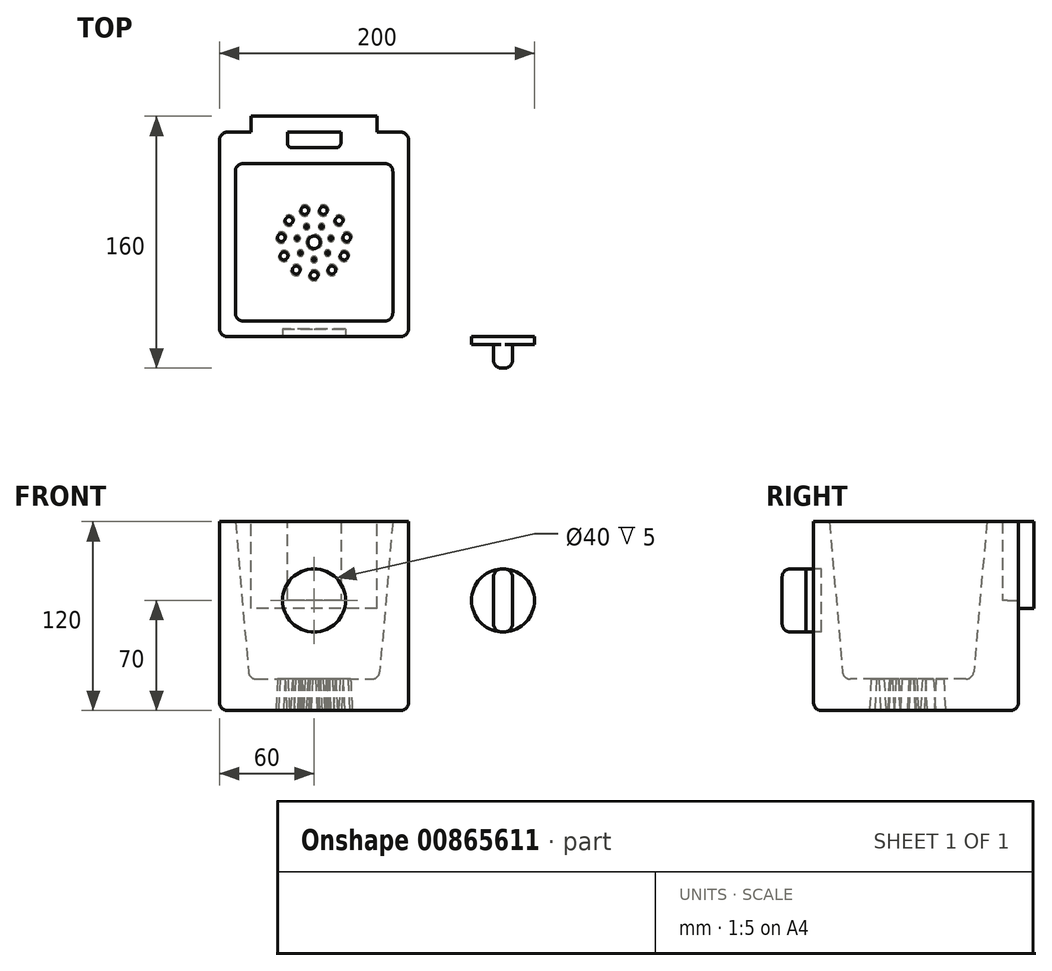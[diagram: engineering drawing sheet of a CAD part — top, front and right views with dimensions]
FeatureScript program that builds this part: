
annotation { "Feature Type Name" : "Feature", "Feature Type Description" : "" }
export const myFeature = defineFeature(function(context is Context, id is Id, definition is map)
    precondition{}
    {
        {
            assignVariable(context, id + "F0", {"name" : "length", "anyValue" : 120});
        }
        {
            var Q0;
            Q0=qCreatedBy(makeId("Top.planeOp"),FACE);
            var sketch = newSketch(context, id + "F1", { "sketchPlane" : qUnion([Q0])});
            skLineSegment(sketch, "E0.bottom", {"start": v(60, 60) * mm, "end": v(-60, 60) * mm});
            skLineSegment(sketch, "E0.top", {"start": v(60, -60) * mm, "end": v(-60, -60) * mm});
            skLineSegment(sketch, "E0.left", {"start": v(60, 60) * mm, "end": v(60, -60) * mm});
            skLineSegment(sketch, "E0.right", {"start": v(-60, 60) * mm, "end": v(-60, -60) * mm});
            skPoint(sketch, "E0.middle", {"position": v(0, 0) * mm});
            skSolve(sketch);
        }
        {
            var Q0;
            Q0=makeQuery(id+"F1.imprint","IMPRINT",FACE,{"disambiguationData":[TD([[makeQuery(id+"F1.imprint","IMPRINT",EDGE,{"derivedFrom":sQuery(id+"F1.wireOp",EDGE,"E0.bottom")}),1.0]])]});
            extrude(context, id + "F2", {"entities" : qUnion([Q0]), "depth" : (getVariable(context, 'length')) * mm, "offsetDistance" : 25 * mm});
        }
        {
            var Q0;
            Q0=makeQuery(id+"F2.opExtrude","SWEPT_FACE",FACE,{"disambiguationData":[OSD([sQuery(id+"F1.wireOp",EDGE,"E0.bottom")])]});
            var sketch = newSketch(context, id + "F3", { "sketchPlane" : qUnion([Q0])});
            skLineSegment(sketch, "E1.bottom", {"start": v(-60, 0) * mm, "end": v(60, 0) * mm});
            skLineSegment(sketch, "E1.top", {"start": v(-60, 216) * mm, "end": v(60, 216) * mm});
            skLineSegment(sketch, "E1.left", {"start": v(-60, 0) * mm, "end": v(-60, 216) * mm});
            skLineSegment(sketch, "E1.right", {"start": v(60, 0) * mm, "end": v(60, 216) * mm});
            skSolve(sketch);
        }
        {
            var Q0;
            Q0=makeQuery(id+"F2.opExtrude","CAP_FACE",FACE,{"disambiguationData":[OSD([sQuery(id+"F1.wireOp",EDGE,"E0.bottom"),sQuery(id+"F1.wireOp",EDGE,"E0.top"),sQuery(id+"F1.wireOp",EDGE,"E0.left"),sQuery(id+"F1.wireOp",EDGE,"E0.right")])],"isStart":false});
            var sketch = newSketch(context, id + "F4", { "sketchPlane" : qUnion([Q0])});
            skLineSegment(sketch, "E2.bottom", {"start": v(50, 50) * mm, "end": v(-50, 50) * mm});
            skLineSegment(sketch, "E2.top", {"start": v(50, -50) * mm, "end": v(-50, -50) * mm});
            skLineSegment(sketch, "E2.left", {"start": v(50, 50) * mm, "end": v(50, -50) * mm});
            skLineSegment(sketch, "E2.right", {"start": v(-50, 50) * mm, "end": v(-50, -50) * mm});
            skPoint(sketch, "E2.middle", {"position": v(0, 0) * mm});
            skSolve(sketch);
        }
        {
            var Q0;
            Q0=makeQuery(id+"F4.imprint","IMPRINT",FACE,{"disambiguationData":[TD([[makeQuery(id+"F4.imprint","IMPRINT",EDGE,{"derivedFrom":sQuery(id+"F4.wireOp",EDGE,"E2.bottom")}),1.0]])]});
            extrude(context, id + "F5", {"entities" : qUnion([Q0]), "operationType" : NewBodyOperationType.REMOVE, "oppositeDirection" : true, "depth" : 100 * mm, "offsetDistance" : 25 * mm, "hasDraft" : true, "draftAngle" : 5 * degree, "draftPullDirection" : true});
        }
        {
            var Q0;
            {var subQ0=sQuery(id+"F3.wireOp",EDGE,"E1.bottom");Q0=makeQuery(id+"F3.imprint","IMPRINT",FACE,{"disambiguationData":[TD([[makeQuery(id+"F3.imprint","IMPRINT",EDGE,{"derivedFrom":subQ0}),1.0]])]});}
            var Q1;
            {var subQ0=sQuery(id+"F3.wireOp",EDGE,"E1.top");Q1=makeQuery(id+"F3.imprint","IMPRINT",FACE,{"disambiguationData":[TD([[makeQuery(id+"F3.imprint","IMPRINT",EDGE,{"derivedFrom":subQ0}),-1.0]])]});}
            extrude(context, id + "F6", {"entities" : qUnion([Q0, Q1]), "operationType" : NewBodyOperationType.ADD, "depth" : 10 * mm, "offsetDistance" : 25 * mm});
        }
        {
            var Q0;
            Q0=makeQuery(id+"F6.opExtrude","CAP_FACE",FACE,{"disambiguationData":[OSD([sQuery(id+"F3.wireOp",EDGE,"E1.bottom"),sQuery(id+"F3.wireOp",EDGE,"E1.top"),sQuery(id+"F3.wireOp",EDGE,"E1.left"),sQuery(id+"F3.wireOp",EDGE,"E1.right")])],"isStart":true});
            var sketch = newSketch(context, id + "F7", { "sketchPlane" : qUnion([Q0])});
            skLineSegment(sketch, "E3", {"start": v(0, 223.83) * mm, "end": v(0, 211) * mm, "construction": true});
            skPoint(sketch, "E3.startSnap0", {"position": v(0, 216) * mm});
            skLineSegment(sketch, "E4.bottom", {"start": v(0, 194) * mm, "end": v(-45, 194) * mm});
            skLineSegment(sketch, "E4.top", {"start": v(0, 184) * mm, "end": v(-45, 184) * mm});
            skLineSegment(sketch, "E4.left", {"start": v(0, 194) * mm, "end": v(0, 184) * mm});
            skLineSegment(sketch, "E4.right", {"start": v(-45, 194) * mm, "end": v(-45, 184) * mm});
            skLineSegment(sketch, "E5.bottom", {"start": v(-45, 179) * mm, "end": v(-20, 179) * mm});
            skLineSegment(sketch, "E5.top", {"start": v(-45, 169) * mm, "end": v(-20, 169) * mm});
            skLineSegment(sketch, "E5.left", {"start": v(-45, 179) * mm, "end": v(-45, 169) * mm});
            skLineSegment(sketch, "E5.right", {"start": v(-20, 179) * mm, "end": v(-20, 169) * mm});
            skLineSegment(sketch, "E6.bottom", {"start": v(-45, 164) * mm, "end": v(0, 164) * mm});
            skLineSegment(sketch, "E6.top", {"start": v(-45, 154) * mm, "end": v(0, 154) * mm});
            skLineSegment(sketch, "E6.left", {"start": v(-45, 164) * mm, "end": v(-45, 154) * mm});
            skLineSegment(sketch, "E6.right", {"start": v(0, 164) * mm, "end": v(0, 154) * mm});
            skLineSegment(sketch, "E7.bottom", {"start": v(-45, 149) * mm, "end": v(-35, 149) * mm});
            skLineSegment(sketch, "E7.top", {"start": v(-45, 129) * mm, "end": v(-35, 129) * mm});
            skLineSegment(sketch, "E7.left", {"start": v(-45, 149) * mm, "end": v(-45, 129) * mm});
            skLineSegment(sketch, "E7.right", {"start": v(-35, 149) * mm, "end": v(-35, 139) * mm});
            skLineSegment(sketch, "E8.bottom", {"start": v(-35, 139) * mm, "end": v(0, 139) * mm});
            skLineSegment(sketch, "E8.top", {"start": v(-35, 129) * mm, "end": v(0, 129) * mm});
            skLineSegment(sketch, "E8.right", {"start": v(0, 139) * mm, "end": v(0, 129) * mm});
            skLineSegment(sketch, "E9.bottom", {"start": v(-28, 149) * mm, "end": v(0, 149) * mm});
            skLineSegment(sketch, "E9.top", {"start": v(-28, 144) * mm, "end": v(0, 144) * mm});
            skLineSegment(sketch, "E9.left", {"start": v(-28, 149) * mm, "end": v(-28, 144) * mm});
            skLineSegment(sketch, "E9.right", {"start": v(0, 149) * mm, "end": v(0, 144) * mm});
            skLineSegment(sketch, "E10.bottom", {"start": v(-45, 211) * mm, "end": v(-35, 211) * mm});
            skLineSegment(sketch, "E10.top", {"start": v(-45, 198) * mm, "end": v(-35, 198) * mm});
            skLineSegment(sketch, "E10.left", {"start": v(-45, 211) * mm, "end": v(-45, 198) * mm});
            skLineSegment(sketch, "E10.right", {"start": v(-35, 211) * mm, "end": v(-35, 198) * mm});
            skLineSegment(sketch, "E11.bottom", {"start": v(0, 211) * mm, "end": v(-25, 211) * mm});
            skLineSegment(sketch, "E11.top", {"start": v(0, 198) * mm, "end": v(-25, 198) * mm});
            skLineSegment(sketch, "E11.left", {"start": v(0, 211) * mm, "end": v(0, 198) * mm});
            skLineSegment(sketch, "E11.right", {"start": v(-25, 211) * mm, "end": v(-25, 198) * mm});
            skArc(sketch, "E12", {"start": v(0, 180.92) * mm, "mid": v(-6.92, 174) * mm, "end": v(0, 167.08) * mm});
            skPoint(sketch, "E12.centerSnap0", {"position": v(-20, 174) * mm});
            skLineSegment(sketch, "E13.trimOffspring", {"start": v(0, 154) * mm, "end": v(0, 149) * mm, "construction": true});
            skLineSegment(sketch, "E14.trimOffspring", {"start": v(0, 144) * mm, "end": v(0, 139) * mm, "construction": true});
            skLineSegment(sketch, "E15.trimOffspring", {"start": v(0, 129) * mm, "end": v(0, 105.75) * mm, "construction": true});
            skLineSegment(sketch, "E16.trimOffspring", {"start": v(0, 184) * mm, "end": v(0, 164) * mm, "construction": true});
            skLineSegment(sketch, "E17.trimOffspring", {"start": v(0, 198) * mm, "end": v(0, 194) * mm, "construction": true});
            skArc(sketch, "E18.MirrorCS", {"start": v(0, 180.92) * mm, "mid": v(6.92, 174) * mm, "end": v(0, 167.08) * mm});
            skLineSegment(sketch, "E19.MirrorCS", {"start": v(28, 149) * mm, "end": v(28, 144) * mm});
            skLineSegment(sketch, "E20.MirrorCS", {"start": v(20, 179) * mm, "end": v(20, 169) * mm});
            skLineSegment(sketch, "E21.MirrorCS", {"start": v(35, 211) * mm, "end": v(35, 198) * mm});
            skLineSegment(sketch, "E22.MirrorCS", {"start": v(45, 169) * mm, "end": v(20, 169) * mm});
            skPoint(sketch, "E23.MirrorP", {"position": v(20, 174) * mm});
            skLineSegment(sketch, "E24.MirrorCS", {"start": v(45, 179) * mm, "end": v(20, 179) * mm});
            skLineSegment(sketch, "E25.MirrorCS", {"start": v(0, 211) * mm, "end": v(25, 211) * mm});
            skLineSegment(sketch, "E26.MirrorCS", {"start": v(28, 144) * mm, "end": v(0, 144) * mm});
            skLineSegment(sketch, "E27.MirrorCS", {"start": v(45, 154) * mm, "end": v(0, 154) * mm});
            skLineSegment(sketch, "E28.MirrorCS", {"start": v(45, 129) * mm, "end": v(35, 129) * mm});
            skLineSegment(sketch, "E29.MirrorCS", {"start": v(45, 179) * mm, "end": v(45, 169) * mm});
            skLineSegment(sketch, "E30.MirrorCS", {"start": v(0, 194) * mm, "end": v(45, 194) * mm});
            skLineSegment(sketch, "E31.MirrorCS", {"start": v(45, 149) * mm, "end": v(35, 149) * mm});
            skLineSegment(sketch, "E32.MirrorCS", {"start": v(35, 149) * mm, "end": v(35, 139) * mm});
            skLineSegment(sketch, "E33.MirrorCS", {"start": v(45, 211) * mm, "end": v(35, 211) * mm});
            skLineSegment(sketch, "E34.MirrorCS", {"start": v(25, 211) * mm, "end": v(25, 198) * mm});
            skLineSegment(sketch, "E35.MirrorCS", {"start": v(45, 198) * mm, "end": v(35, 198) * mm});
            skLineSegment(sketch, "E36.MirrorCS", {"start": v(35, 129) * mm, "end": v(0, 129) * mm});
            skLineSegment(sketch, "E37.MirrorCS", {"start": v(45, 164) * mm, "end": v(0, 164) * mm});
            skLineSegment(sketch, "E38.MirrorCS", {"start": v(35, 139) * mm, "end": v(0, 139) * mm});
            skLineSegment(sketch, "E39.MirrorCS", {"start": v(28, 149) * mm, "end": v(0, 149) * mm});
            skLineSegment(sketch, "E40.MirrorCS", {"start": v(0, 184) * mm, "end": v(45, 184) * mm});
            skLineSegment(sketch, "E41.MirrorCS", {"start": v(45, 164) * mm, "end": v(45, 154) * mm});
            skLineSegment(sketch, "E42.MirrorCS", {"start": v(45, 211) * mm, "end": v(45, 198) * mm});
            skLineSegment(sketch, "E43.MirrorCS", {"start": v(0, 198) * mm, "end": v(25, 198) * mm});
            skLineSegment(sketch, "E44.MirrorCS", {"start": v(45, 149) * mm, "end": v(45, 129) * mm});
            skLineSegment(sketch, "E45.MirrorCS", {"start": v(45, 194) * mm, "end": v(45, 184) * mm});
            skSolve(sketch);
        }
        {
            var Q0;
            Q0=makeQuery(id+"F7.imprint","IMPRINT",FACE,{"disambiguationData":[TD([[makeQuery(id+"F7.imprint","IMPRINT",EDGE,{"derivedFrom":sQuery(id+"F7.wireOp",EDGE,"E7.bottom")}),-1.0]])]});
            var Q1;
            Q1=makeQuery(id+"F7.imprint","IMPRINT",FACE,{"disambiguationData":[TD([[makeQuery(id+"F7.imprint","IMPRINT",EDGE,{"derivedFrom":sQuery(id+"F7.wireOp",EDGE,"E9.bottom")}),-1.0]])]});
            var Q2;
            Q2=makeQuery(id+"F7.imprint","IMPRINT",FACE,{"disambiguationData":[TD([[makeQuery(id+"F7.imprint","IMPRINT",EDGE,{"derivedFrom":sQuery(id+"F7.wireOp",EDGE,"E8.right")}),1.0]])]});
            var Q3;
            Q3=makeQuery(id+"F7.imprint","IMPRINT",FACE,{"disambiguationData":[TD([[makeQuery(id+"F7.imprint","IMPRINT",EDGE,{"derivedFrom":sQuery(id+"F7.wireOp",EDGE,"E9.right")}),1.0]])]});
            var Q4;
            Q4=makeQuery(id+"F7.imprint","IMPRINT",FACE,{"disambiguationData":[TD([[makeQuery(id+"F7.imprint","IMPRINT",EDGE,{"derivedFrom":sQuery(id+"F7.wireOp",EDGE,"E6.bottom")}),-1.0]])]});
            var Q5;
            Q5=makeQuery(id+"F7.imprint","IMPRINT",FACE,{"disambiguationData":[TD([[makeQuery(id+"F7.imprint","IMPRINT",EDGE,{"derivedFrom":sQuery(id+"F7.wireOp",EDGE,"E5.bottom")}),-1.0]])]});
            var Q6;
            Q6=makeQuery(id+"F7.imprint","IMPRINT",FACE,{"disambiguationData":[TD([[makeQuery(id+"F7.imprint","IMPRINT",EDGE,{"derivedFrom":sQuery(id+"F7.wireOp",EDGE,"E4.bottom")}),1.0]])]});
            var Q7;
            Q7=makeQuery(id+"F7.imprint","IMPRINT",FACE,{"disambiguationData":[TD([[makeQuery(id+"F7.imprint","IMPRINT",EDGE,{"derivedFrom":sQuery(id+"F7.wireOp",EDGE,"E10.bottom")}),-1.0]])]});
            var Q8;
            Q8=makeQuery(id+"F7.imprint","IMPRINT",FACE,{"disambiguationData":[TD([[makeQuery(id+"F7.imprint","IMPRINT",EDGE,{"derivedFrom":sQuery(id+"F7.wireOp",EDGE,"E11.bottom")}),1.0]])]});
            var Q9;
            Q9=makeQuery(id+"F7.imprint","IMPRINT",FACE,{"disambiguationData":[TD([[makeQuery(id+"F7.imprint","IMPRINT",EDGE,{"derivedFrom":sQuery(id+"F7.wireOp",EDGE,"E11.left")}),1.0]])]});
            var Q10;
            Q10=makeQuery(id+"F7.imprint","IMPRINT",FACE,{"disambiguationData":[TD([[makeQuery(id+"F7.imprint","IMPRINT",EDGE,{"derivedFrom":sQuery(id+"F7.wireOp",EDGE,"E21.MirrorCS")}),1.0]])]});
            var Q11;
            Q11=makeQuery(id+"F7.imprint","IMPRINT",FACE,{"disambiguationData":[TD([[makeQuery(id+"F7.imprint","IMPRINT",EDGE,{"derivedFrom":sQuery(id+"F7.wireOp",EDGE,"E4.left")}),1.0]])]});
            var Q12;
            Q12=makeQuery(id+"F7.imprint","IMPRINT",FACE,{"disambiguationData":[TD([[makeQuery(id+"F7.imprint","IMPRINT",EDGE,{"derivedFrom":sQuery(id+"F7.wireOp",EDGE,"E20.MirrorCS")}),1.0]])]});
            var Q13;
            Q13=makeQuery(id+"F7.imprint","IMPRINT",FACE,{"disambiguationData":[TD([[makeQuery(id+"F7.imprint","IMPRINT",EDGE,{"derivedFrom":sQuery(id+"F7.wireOp",EDGE,"E12")}),1.0]])]});
            var Q14;
            Q14=makeQuery(id+"F7.imprint","IMPRINT",FACE,{"disambiguationData":[TD([[makeQuery(id+"F7.imprint","IMPRINT",EDGE,{"derivedFrom":sQuery(id+"F7.wireOp",EDGE,"E6.right")}),1.0]])]});
            var Q15;
            Q15=makeQuery(id+"F6.opExtrude","CAP_FACE",FACE,{"disambiguationData":[OSD([sQuery(id+"F3.wireOp",EDGE,"E1.bottom"),sQuery(id+"F3.wireOp",EDGE,"E1.top"),sQuery(id+"F3.wireOp",EDGE,"E1.left"),sQuery(id+"F3.wireOp",EDGE,"E1.right")])],"isStart":false});
            extrude(context, id + "F8", {"entities" : qUnion([Q0, Q1, Q2, Q3, Q4, Q5, Q6, Q7, Q8, Q9, Q10, Q11, Q12, Q13, Q14]), "operationType" : NewBodyOperationType.REMOVE, "endBound" : BoundingType.UP_TO_SURFACE, "oppositeDirection" : true, "depth" : 25 * mm, "endBoundEntityFace" : qUnion([Q15]), "offsetDistance" : 25 * mm});
        }
        {
            var Q0;
            Q0=makeQuery(id+"F6.opExtrude","SWEPT_FACE",FACE,{"disambiguationData":[OSD([sQuery(id+"F3.wireOp",EDGE,"E1.top")])]});
            var sketch = newSketch(context, id + "F9", { "sketchPlane" : qUnion([Q0])});
            skLineSegment(sketch, "E46.bottom", {"start": v(-60, 70) * mm, "end": v(60, 70) * mm});
            skLineSegment(sketch, "E46.top", {"start": v(-60, -60) * mm, "end": v(60, -60) * mm});
            skLineSegment(sketch, "E46.left", {"start": v(-60, 70) * mm, "end": v(-60, -60) * mm});
            skLineSegment(sketch, "E46.right", {"start": v(60, 70) * mm, "end": v(60, -60) * mm});
            skSolve(sketch);
        }
        {
            var Q0;
            Q0=qSketchRegion(id+"F9",true);
            extrude(context, id + "F10", {"entities" : qUnion([Q0]), "operationType" : NewBodyOperationType.ADD, "depth" : 25 * mm, "offsetDistance" : 25 * mm, "hasDraft" : true, "draftAngle" : 10 * degree, "draftPullDirection" : true});
        }
        {
            var Q0;
            Q0=makeQuery(id+"F10.opExtrude","CAP_FACE",FACE,{"disambiguationData":[OSD([sQuery(id+"F9.wireOp",EDGE,"E46.bottom"),sQuery(id+"F9.wireOp",EDGE,"E46.top"),sQuery(id+"F9.wireOp",EDGE,"E46.left"),sQuery(id+"F9.wireOp",EDGE,"E46.right")])],"isStart":false});
            var sketch = newSketch(context, id + "F11", { "sketchPlane" : qUnion([Q0])});
            skLineSegment(sketch, "E47.bottom", {"start": v(-45.6, 55.6) * mm, "end": v(45.6, 55.6) * mm});
            skLineSegment(sketch, "E47.top", {"start": v(-45.6, -45.6) * mm, "end": v(45.6, -45.6) * mm});
            skLineSegment(sketch, "E47.left", {"start": v(-45.6, 55.6) * mm, "end": v(-45.6, -45.6) * mm});
            skLineSegment(sketch, "E47.right", {"start": v(45.6, 55.6) * mm, "end": v(45.6, -45.6) * mm});
            skSolve(sketch);
        }
        {
            var Q0;
            Q0=makeQuery(id+"F11.imprint","IMPRINT",FACE,{"disambiguationData":[TD([[makeQuery(id+"F11.imprint","IMPRINT",EDGE,{"derivedFrom":sQuery(id+"F11.wireOp",EDGE,"E47.bottom")}),-1.0]])]});
            extrude(context, id + "F12", {"entities" : qUnion([Q0]), "operationType" : NewBodyOperationType.REMOVE, "oppositeDirection" : true, "depth" : 10 * mm, "offsetDistance" : 25 * mm, "hasDraft" : true, "draftAngle" : 7 * degree, "draftPullDirection" : true});
        }
        {
            var Q0;
            Q0=makeQuery(id+"F12.boolean.opBoolean","COPY",FACE,{"derivedFrom":makeQuery(id+"F12.opExtrude","CAP_FACE",FACE,{"disambiguationData":[OSD([sQuery(id+"F11.wireOp",EDGE,"E47.bottom"),sQuery(id+"F11.wireOp",EDGE,"E47.top"),sQuery(id+"F11.wireOp",EDGE,"E47.left"),sQuery(id+"F11.wireOp",EDGE,"E47.right")])],"isStart":false})});
            var sketch = newSketch(context, id + "F13", { "sketchPlane" : qUnion([Q0])});
            skLineSegment(sketch, "E48.bottom", {"start": v(-44.36, 54.36) * mm, "end": v(44.36, 54.36) * mm});
            skLineSegment(sketch, "E48.top", {"start": v(-44.36, 51.36) * mm, "end": v(44.36, 51.36) * mm});
            skLineSegment(sketch, "E48.left", {"start": v(-44.36, 54.36) * mm, "end": v(-44.36, 51.36) * mm});
            skLineSegment(sketch, "E48.right", {"start": v(44.36, 54.36) * mm, "end": v(44.36, 51.36) * mm});
            skLineSegment(sketch, "E49.0.1.0", {"start": v(-44.36, 46.36) * mm, "end": v(44.36, 46.36) * mm});
            skLineSegment(sketch, "E49.0.1.1", {"start": v(44.36, 49.36) * mm, "end": v(44.36, 46.36) * mm});
            skLineSegment(sketch, "E49.0.1.2", {"start": v(-44.36, 49.36) * mm, "end": v(44.36, 49.36) * mm});
            skLineSegment(sketch, "E49.0.1.3", {"start": v(-44.36, 49.36) * mm, "end": v(-44.36, 46.36) * mm});
            skLineSegment(sketch, "E49.0.2.0", {"start": v(-44.36, 41.36) * mm, "end": v(44.36, 41.36) * mm});
            skLineSegment(sketch, "E49.0.2.1", {"start": v(44.36, 44.36) * mm, "end": v(44.36, 41.36) * mm});
            skLineSegment(sketch, "E49.0.2.2", {"start": v(-44.36, 44.36) * mm, "end": v(44.36, 44.36) * mm});
            skLineSegment(sketch, "E49.0.2.3", {"start": v(-44.36, 44.36) * mm, "end": v(-44.36, 41.36) * mm});
            skLineSegment(sketch, "E49.0.3.0", {"start": v(-44.36, 36.36) * mm, "end": v(44.36, 36.36) * mm});
            skLineSegment(sketch, "E49.0.3.1", {"start": v(44.36, 39.36) * mm, "end": v(44.36, 36.36) * mm});
            skLineSegment(sketch, "E49.0.3.2", {"start": v(-44.36, 39.36) * mm, "end": v(44.36, 39.36) * mm});
            skLineSegment(sketch, "E49.0.3.3", {"start": v(-44.36, 39.36) * mm, "end": v(-44.36, 36.36) * mm});
            skLineSegment(sketch, "E49.0.4.0", {"start": v(-44.36, 31.36) * mm, "end": v(44.36, 31.36) * mm});
            skLineSegment(sketch, "E49.0.4.1", {"start": v(44.36, 34.36) * mm, "end": v(44.36, 31.36) * mm});
            skLineSegment(sketch, "E49.0.4.2", {"start": v(-44.36, 34.36) * mm, "end": v(44.36, 34.36) * mm});
            skLineSegment(sketch, "E49.0.4.3", {"start": v(-44.36, 34.36) * mm, "end": v(-44.36, 31.36) * mm});
            skLineSegment(sketch, "E49.0.5.0", {"start": v(-44.36, 26.36) * mm, "end": v(44.36, 26.36) * mm});
            skLineSegment(sketch, "E49.0.5.1", {"start": v(44.36, 29.36) * mm, "end": v(44.36, 26.36) * mm});
            skLineSegment(sketch, "E49.0.5.2", {"start": v(-44.36, 29.36) * mm, "end": v(44.36, 29.36) * mm});
            skLineSegment(sketch, "E49.0.5.3", {"start": v(-44.36, 29.36) * mm, "end": v(-44.36, 26.36) * mm});
            skLineSegment(sketch, "E49.0.6.0", {"start": v(-44.36, 21.36) * mm, "end": v(44.36, 21.36) * mm});
            skLineSegment(sketch, "E49.0.6.1", {"start": v(44.36, 24.36) * mm, "end": v(44.36, 21.36) * mm});
            skLineSegment(sketch, "E49.0.6.2", {"start": v(-44.36, 24.36) * mm, "end": v(44.36, 24.36) * mm});
            skLineSegment(sketch, "E49.0.6.3", {"start": v(-44.36, 24.36) * mm, "end": v(-44.36, 21.36) * mm});
            skLineSegment(sketch, "E49.0.7.0", {"start": v(-44.36, 16.36) * mm, "end": v(44.36, 16.36) * mm});
            skLineSegment(sketch, "E49.0.7.1", {"start": v(44.36, 19.36) * mm, "end": v(44.36, 16.36) * mm});
            skLineSegment(sketch, "E49.0.7.2", {"start": v(-44.36, 19.36) * mm, "end": v(44.36, 19.36) * mm});
            skLineSegment(sketch, "E49.0.7.3", {"start": v(-44.36, 19.36) * mm, "end": v(-44.36, 16.36) * mm});
            skLineSegment(sketch, "E49.0.8.0", {"start": v(-44.36, 11.36) * mm, "end": v(44.36, 11.36) * mm});
            skLineSegment(sketch, "E49.0.8.1", {"start": v(44.36, 14.36) * mm, "end": v(44.36, 11.36) * mm});
            skLineSegment(sketch, "E49.0.8.2", {"start": v(-44.36, 14.36) * mm, "end": v(44.36, 14.36) * mm});
            skLineSegment(sketch, "E49.0.8.3", {"start": v(-44.36, 14.36) * mm, "end": v(-44.36, 11.36) * mm});
            skLineSegment(sketch, "E49.0.9.0", {"start": v(-44.36, 6.36) * mm, "end": v(44.36, 6.36) * mm});
            skLineSegment(sketch, "E49.0.9.1", {"start": v(44.36, 9.36) * mm, "end": v(44.36, 6.36) * mm});
            skLineSegment(sketch, "E49.0.9.2", {"start": v(-44.36, 9.36) * mm, "end": v(44.36, 9.36) * mm});
            skLineSegment(sketch, "E49.0.9.3", {"start": v(-44.36, 9.36) * mm, "end": v(-44.36, 6.36) * mm});
            skLineSegment(sketch, "E49.0.10.0", {"start": v(-44.36, 1.36) * mm, "end": v(44.36, 1.36) * mm});
            skLineSegment(sketch, "E49.0.10.1", {"start": v(44.36, 4.36) * mm, "end": v(44.36, 1.36) * mm});
            skLineSegment(sketch, "E49.0.10.2", {"start": v(-44.36, 4.36) * mm, "end": v(44.36, 4.36) * mm});
            skLineSegment(sketch, "E49.0.10.3", {"start": v(-44.36, 4.36) * mm, "end": v(-44.36, 1.36) * mm});
            skLineSegment(sketch, "E49.0.11.0", {"start": v(-44.36, -3.64) * mm, "end": v(44.36, -3.64) * mm});
            skLineSegment(sketch, "E49.0.11.1", {"start": v(44.36, -0.64) * mm, "end": v(44.36, -3.64) * mm});
            skLineSegment(sketch, "E49.0.11.2", {"start": v(-44.36, -0.64) * mm, "end": v(44.36, -0.64) * mm});
            skLineSegment(sketch, "E49.0.11.3", {"start": v(-44.36, -0.64) * mm, "end": v(-44.36, -3.64) * mm});
            skLineSegment(sketch, "E49.0.12.0", {"start": v(-44.36, -8.64) * mm, "end": v(44.36, -8.64) * mm});
            skLineSegment(sketch, "E49.0.12.1", {"start": v(44.36, -5.64) * mm, "end": v(44.36, -8.64) * mm});
            skLineSegment(sketch, "E49.0.12.2", {"start": v(-44.36, -5.64) * mm, "end": v(44.36, -5.64) * mm});
            skLineSegment(sketch, "E49.0.12.3", {"start": v(-44.36, -5.64) * mm, "end": v(-44.36, -8.64) * mm});
            skLineSegment(sketch, "E49.0.13.0", {"start": v(-44.36, -13.64) * mm, "end": v(44.36, -13.64) * mm});
            skLineSegment(sketch, "E49.0.13.1", {"start": v(44.36, -10.64) * mm, "end": v(44.36, -13.64) * mm});
            skLineSegment(sketch, "E49.0.13.2", {"start": v(-44.36, -10.64) * mm, "end": v(44.36, -10.64) * mm});
            skLineSegment(sketch, "E49.0.13.3", {"start": v(-44.36, -10.64) * mm, "end": v(-44.36, -13.64) * mm});
            skLineSegment(sketch, "E49.0.14.0", {"start": v(-44.36, -18.64) * mm, "end": v(44.36, -18.64) * mm});
            skLineSegment(sketch, "E49.0.14.1", {"start": v(44.36, -15.64) * mm, "end": v(44.36, -18.64) * mm});
            skLineSegment(sketch, "E49.0.14.2", {"start": v(-44.36, -15.64) * mm, "end": v(44.36, -15.64) * mm});
            skLineSegment(sketch, "E49.0.14.3", {"start": v(-44.36, -15.64) * mm, "end": v(-44.36, -18.64) * mm});
            skLineSegment(sketch, "E49.0.15.0", {"start": v(-44.36, -23.64) * mm, "end": v(44.36, -23.64) * mm});
            skLineSegment(sketch, "E49.0.15.1", {"start": v(44.36, -20.64) * mm, "end": v(44.36, -23.64) * mm});
            skLineSegment(sketch, "E49.0.15.2", {"start": v(-44.36, -20.64) * mm, "end": v(44.36, -20.64) * mm});
            skLineSegment(sketch, "E49.0.15.3", {"start": v(-44.36, -20.64) * mm, "end": v(-44.36, -23.64) * mm});
            skLineSegment(sketch, "E49.0.16.0", {"start": v(-44.36, -28.64) * mm, "end": v(44.36, -28.64) * mm});
            skLineSegment(sketch, "E49.0.16.1", {"start": v(44.36, -25.64) * mm, "end": v(44.36, -28.64) * mm});
            skLineSegment(sketch, "E49.0.16.2", {"start": v(-44.36, -25.64) * mm, "end": v(44.36, -25.64) * mm});
            skLineSegment(sketch, "E49.0.16.3", {"start": v(-44.36, -25.64) * mm, "end": v(-44.36, -28.64) * mm});
            skLineSegment(sketch, "E49.0.17.0", {"start": v(-44.36, -33.64) * mm, "end": v(44.36, -33.64) * mm});
            skLineSegment(sketch, "E49.0.17.1", {"start": v(44.36, -30.64) * mm, "end": v(44.36, -33.64) * mm});
            skLineSegment(sketch, "E49.0.17.2", {"start": v(-44.36, -30.64) * mm, "end": v(44.36, -30.64) * mm});
            skLineSegment(sketch, "E49.0.17.3", {"start": v(-44.36, -30.64) * mm, "end": v(-44.36, -33.64) * mm});
            skLineSegment(sketch, "E49.0.18.0", {"start": v(-44.36, -38.64) * mm, "end": v(44.36, -38.64) * mm});
            skLineSegment(sketch, "E49.0.18.1", {"start": v(44.36, -35.64) * mm, "end": v(44.36, -38.64) * mm});
            skLineSegment(sketch, "E49.0.18.2", {"start": v(-44.36, -35.64) * mm, "end": v(44.36, -35.64) * mm});
            skLineSegment(sketch, "E49.0.18.3", {"start": v(-44.36, -35.64) * mm, "end": v(-44.36, -38.64) * mm});
            skLineSegment(sketch, "E49.direction1", {"start": v(-44.36, 51.36) * mm, "end": v(-19.36, 51.36) * mm, "construction": true});
            skLineSegment(sketch, "E49.direction2", {"start": v(-44.36, 51.36) * mm, "end": v(-44.36, 46.36) * mm, "construction": true});
            skLineSegment(sketch, "E50.0.0.19", {"start": v(-44.36, -43.64) * mm, "end": v(44.36, -43.64) * mm});
            skLineSegment(sketch, "E50.3.0.19", {"start": v(44.36, -40.64) * mm, "end": v(44.36, -43.64) * mm});
            skLineSegment(sketch, "E50.6.0.19", {"start": v(-44.36, -40.64) * mm, "end": v(44.36, -40.64) * mm});
            skLineSegment(sketch, "E50.9.0.19", {"start": v(-44.36, -40.64) * mm, "end": v(-44.36, -43.64) * mm});
            skSolve(sketch);
        }
        {
            var Q0;
            Q0=qSketchRegion(id+"F13",true);
            var Q1;
            Q1=makeQuery(id+"F10.opExtrude","CAP_FACE",FACE,{"disambiguationData":[OSD([sQuery(id+"F9.wireOp",EDGE,"E46.bottom"),sQuery(id+"F9.wireOp",EDGE,"E46.top"),sQuery(id+"F9.wireOp",EDGE,"E46.left"),sQuery(id+"F9.wireOp",EDGE,"E46.right")])],"isStart":true});
            extrude(context, id + "F14", {"entities" : qUnion([Q0]), "operationType" : NewBodyOperationType.REMOVE, "endBound" : BoundingType.UP_TO_SURFACE, "oppositeDirection" : true, "depth" : 25 * mm, "endBoundEntityFace" : qUnion([Q1]), "offsetDistance" : 25 * mm});
        }
        {
            var Q0;
            Q0=makeQuery(id+"F14.boolean.opBoolean","COPY",EDGE,{"derivedFrom":makeQuery(id+"F14.opExtrude","CAP_EDGE",EDGE,{"disambiguationData":[OSD([sQuery(id+"F13.wireOp",EDGE,"E48.top")])],"isStart":true})});
            var Q1;
            Q1=makeQuery(id+"F14.boolean.opBoolean","COPY",EDGE,{"derivedFrom":makeQuery(id+"F14.opExtrude","CAP_EDGE",EDGE,{"disambiguationData":[OSD([sQuery(id+"F13.wireOp",EDGE,"E49.0.1.2")])],"isStart":true})});
            var Q2;
            Q2=makeQuery(id+"F14.boolean.opBoolean","COPY",EDGE,{"derivedFrom":makeQuery(id+"F14.opExtrude","CAP_EDGE",EDGE,{"disambiguationData":[OSD([sQuery(id+"F13.wireOp",EDGE,"E49.0.1.0")])],"isStart":true})});
            var Q3;
            Q3=makeQuery(id+"F14.boolean.opBoolean","COPY",EDGE,{"derivedFrom":makeQuery(id+"F14.opExtrude","CAP_EDGE",EDGE,{"disambiguationData":[OSD([sQuery(id+"F13.wireOp",EDGE,"E49.0.2.2")])],"isStart":true})});
            var Q4;
            Q4=makeQuery(id+"F14.boolean.opBoolean","COPY",EDGE,{"derivedFrom":makeQuery(id+"F14.opExtrude","CAP_EDGE",EDGE,{"disambiguationData":[OSD([sQuery(id+"F13.wireOp",EDGE,"E49.0.2.0")])],"isStart":true})});
            var Q5;
            Q5=makeQuery(id+"F14.boolean.opBoolean","COPY",EDGE,{"derivedFrom":makeQuery(id+"F14.opExtrude","CAP_EDGE",EDGE,{"disambiguationData":[OSD([sQuery(id+"F13.wireOp",EDGE,"E49.0.3.2")])],"isStart":true})});
            var Q6;
            Q6=makeQuery(id+"F14.boolean.opBoolean","COPY",EDGE,{"derivedFrom":makeQuery(id+"F14.opExtrude","CAP_EDGE",EDGE,{"disambiguationData":[OSD([sQuery(id+"F13.wireOp",EDGE,"E49.0.3.0")])],"isStart":true})});
            var Q7;
            Q7=makeQuery(id+"F14.boolean.opBoolean","COPY",EDGE,{"derivedFrom":makeQuery(id+"F14.opExtrude","CAP_EDGE",EDGE,{"disambiguationData":[OSD([sQuery(id+"F13.wireOp",EDGE,"E49.0.4.2")])],"isStart":true})});
            var Q8;
            Q8=makeQuery(id+"F14.boolean.opBoolean","COPY",EDGE,{"derivedFrom":makeQuery(id+"F14.opExtrude","CAP_EDGE",EDGE,{"disambiguationData":[OSD([sQuery(id+"F13.wireOp",EDGE,"E49.0.4.0")])],"isStart":true})});
            var Q9;
            Q9=makeQuery(id+"F14.boolean.opBoolean","COPY",EDGE,{"derivedFrom":makeQuery(id+"F14.opExtrude","CAP_EDGE",EDGE,{"disambiguationData":[OSD([sQuery(id+"F13.wireOp",EDGE,"E49.0.5.2")])],"isStart":true})});
            var Q10;
            Q10=makeQuery(id+"F14.boolean.opBoolean","COPY",EDGE,{"derivedFrom":makeQuery(id+"F14.opExtrude","CAP_EDGE",EDGE,{"disambiguationData":[OSD([sQuery(id+"F13.wireOp",EDGE,"E49.0.5.0")])],"isStart":true})});
            var Q11;
            Q11=makeQuery(id+"F14.boolean.opBoolean","COPY",EDGE,{"derivedFrom":makeQuery(id+"F14.opExtrude","CAP_EDGE",EDGE,{"disambiguationData":[OSD([sQuery(id+"F13.wireOp",EDGE,"E49.0.6.2")])],"isStart":true})});
            var Q12;
            Q12=makeQuery(id+"F14.boolean.opBoolean","COPY",EDGE,{"derivedFrom":makeQuery(id+"F14.opExtrude","CAP_EDGE",EDGE,{"disambiguationData":[OSD([sQuery(id+"F13.wireOp",EDGE,"E49.0.6.0")])],"isStart":true})});
            var Q13;
            Q13=makeQuery(id+"F14.boolean.opBoolean","COPY",EDGE,{"derivedFrom":makeQuery(id+"F14.opExtrude","CAP_EDGE",EDGE,{"disambiguationData":[OSD([sQuery(id+"F13.wireOp",EDGE,"E49.0.7.2")])],"isStart":true})});
            var Q14;
            Q14=makeQuery(id+"F14.boolean.opBoolean","COPY",EDGE,{"derivedFrom":makeQuery(id+"F14.opExtrude","CAP_EDGE",EDGE,{"disambiguationData":[OSD([sQuery(id+"F13.wireOp",EDGE,"E49.0.7.0")])],"isStart":true})});
            var Q15;
            Q15=makeQuery(id+"F14.boolean.opBoolean","COPY",EDGE,{"derivedFrom":makeQuery(id+"F14.opExtrude","CAP_EDGE",EDGE,{"disambiguationData":[OSD([sQuery(id+"F13.wireOp",EDGE,"E49.0.8.2")])],"isStart":true})});
            var Q16;
            Q16=makeQuery(id+"F14.boolean.opBoolean","COPY",EDGE,{"derivedFrom":makeQuery(id+"F14.opExtrude","CAP_EDGE",EDGE,{"disambiguationData":[OSD([sQuery(id+"F13.wireOp",EDGE,"E49.0.8.0")])],"isStart":true})});
            var Q17;
            Q17=makeQuery(id+"F14.boolean.opBoolean","COPY",EDGE,{"derivedFrom":makeQuery(id+"F14.opExtrude","CAP_EDGE",EDGE,{"disambiguationData":[OSD([sQuery(id+"F13.wireOp",EDGE,"E49.0.9.2")])],"isStart":true})});
            var Q18;
            Q18=makeQuery(id+"F14.boolean.opBoolean","COPY",EDGE,{"derivedFrom":makeQuery(id+"F14.opExtrude","CAP_EDGE",EDGE,{"disambiguationData":[OSD([sQuery(id+"F13.wireOp",EDGE,"E49.0.12.2")])],"isStart":true})});
            var Q19;
            Q19=makeQuery(id+"F14.boolean.opBoolean","COPY",EDGE,{"derivedFrom":makeQuery(id+"F14.opExtrude","CAP_EDGE",EDGE,{"disambiguationData":[OSD([sQuery(id+"F13.wireOp",EDGE,"E49.0.12.0")])],"isStart":true})});
            var Q20;
            Q20=makeQuery(id+"F14.boolean.opBoolean","COPY",EDGE,{"derivedFrom":makeQuery(id+"F14.opExtrude","CAP_EDGE",EDGE,{"disambiguationData":[OSD([sQuery(id+"F13.wireOp",EDGE,"E49.0.13.2")])],"isStart":true})});
            var Q21;
            Q21=makeQuery(id+"F14.boolean.opBoolean","COPY",EDGE,{"derivedFrom":makeQuery(id+"F14.opExtrude","CAP_EDGE",EDGE,{"disambiguationData":[OSD([sQuery(id+"F13.wireOp",EDGE,"E49.0.13.0")])],"isStart":true})});
            var Q22;
            Q22=makeQuery(id+"F14.boolean.opBoolean","COPY",EDGE,{"derivedFrom":makeQuery(id+"F14.opExtrude","CAP_EDGE",EDGE,{"disambiguationData":[OSD([sQuery(id+"F13.wireOp",EDGE,"E49.0.14.2")])],"isStart":true})});
            var Q23;
            Q23=makeQuery(id+"F14.boolean.opBoolean","COPY",EDGE,{"derivedFrom":makeQuery(id+"F14.opExtrude","CAP_EDGE",EDGE,{"disambiguationData":[OSD([sQuery(id+"F13.wireOp",EDGE,"E49.0.14.0")])],"isStart":true})});
            var Q24;
            Q24=makeQuery(id+"F14.boolean.opBoolean","COPY",EDGE,{"derivedFrom":makeQuery(id+"F14.opExtrude","CAP_EDGE",EDGE,{"disambiguationData":[OSD([sQuery(id+"F13.wireOp",EDGE,"E49.0.15.2")])],"isStart":true})});
            var Q25;
            Q25=makeQuery(id+"F14.boolean.opBoolean","COPY",EDGE,{"derivedFrom":makeQuery(id+"F14.opExtrude","CAP_EDGE",EDGE,{"disambiguationData":[OSD([sQuery(id+"F13.wireOp",EDGE,"E49.0.15.0")])],"isStart":true})});
            var Q26;
            Q26=makeQuery(id+"F14.boolean.opBoolean","COPY",EDGE,{"derivedFrom":makeQuery(id+"F14.opExtrude","CAP_EDGE",EDGE,{"disambiguationData":[OSD([sQuery(id+"F13.wireOp",EDGE,"E49.0.16.2")])],"isStart":true})});
            var Q27;
            Q27=makeQuery(id+"F14.boolean.opBoolean","COPY",EDGE,{"derivedFrom":makeQuery(id+"F14.opExtrude","CAP_EDGE",EDGE,{"disambiguationData":[OSD([sQuery(id+"F13.wireOp",EDGE,"E49.0.16.0")])],"isStart":true})});
            var Q28;
            Q28=makeQuery(id+"F14.boolean.opBoolean","COPY",EDGE,{"derivedFrom":makeQuery(id+"F14.opExtrude","CAP_EDGE",EDGE,{"disambiguationData":[OSD([sQuery(id+"F13.wireOp",EDGE,"E49.0.17.2")])],"isStart":true})});
            var Q29;
            Q29=makeQuery(id+"F14.boolean.opBoolean","COPY",EDGE,{"derivedFrom":makeQuery(id+"F14.opExtrude","CAP_EDGE",EDGE,{"disambiguationData":[OSD([sQuery(id+"F13.wireOp",EDGE,"E49.0.11.0")])],"isStart":true})});
            var Q30;
            Q30=makeQuery(id+"F14.boolean.opBoolean","COPY",EDGE,{"derivedFrom":makeQuery(id+"F14.opExtrude","CAP_EDGE",EDGE,{"disambiguationData":[OSD([sQuery(id+"F13.wireOp",EDGE,"E49.0.11.2")])],"isStart":true})});
            var Q31;
            Q31=makeQuery(id+"F14.boolean.opBoolean","COPY",EDGE,{"derivedFrom":makeQuery(id+"F14.opExtrude","CAP_EDGE",EDGE,{"disambiguationData":[OSD([sQuery(id+"F13.wireOp",EDGE,"E49.0.10.0")])],"isStart":true})});
            var Q32;
            Q32=makeQuery(id+"F14.boolean.opBoolean","COPY",EDGE,{"derivedFrom":makeQuery(id+"F14.opExtrude","CAP_EDGE",EDGE,{"disambiguationData":[OSD([sQuery(id+"F13.wireOp",EDGE,"E49.0.10.2")])],"isStart":true})});
            var Q33;
            Q33=makeQuery(id+"F14.boolean.opBoolean","COPY",EDGE,{"derivedFrom":makeQuery(id+"F14.opExtrude","CAP_EDGE",EDGE,{"disambiguationData":[OSD([sQuery(id+"F13.wireOp",EDGE,"E49.0.9.0")])],"isStart":true})});
            var Q34;
            Q34=makeQuery(id+"F14.boolean.opBoolean","COPY",EDGE,{"derivedFrom":makeQuery(id+"F14.opExtrude","CAP_EDGE",EDGE,{"disambiguationData":[OSD([sQuery(id+"F13.wireOp",EDGE,"E49.0.18.2")])],"isStart":true})});
            var Q35;
            Q35=makeQuery(id+"F14.boolean.opBoolean","COPY",EDGE,{"derivedFrom":makeQuery(id+"F14.opExtrude","CAP_EDGE",EDGE,{"disambiguationData":[OSD([sQuery(id+"F13.wireOp",EDGE,"E49.0.17.0")])],"isStart":true})});
            var Q36;
            Q36=makeQuery(id+"F14.boolean.opBoolean","COPY",EDGE,{"derivedFrom":makeQuery(id+"F14.opExtrude","CAP_EDGE",EDGE,{"disambiguationData":[OSD([sQuery(id+"F13.wireOp",EDGE,"E50.6.0.19")])],"isStart":true})});
            var Q37;
            Q37=makeQuery(id+"F14.boolean.opBoolean","COPY",EDGE,{"derivedFrom":makeQuery(id+"F14.opExtrude","CAP_EDGE",EDGE,{"disambiguationData":[OSD([sQuery(id+"F13.wireOp",EDGE,"E49.0.18.0")])],"isStart":true})});
            var Q38;
            Q38=makeQuery(id+"F14.boolean.opBoolean","COPY",EDGE,{"derivedFrom":makeQuery(id+"F14.opExtrude","CAP_EDGE",EDGE,{"disambiguationData":[OSD([sQuery(id+"F13.wireOp",EDGE,"E50.0.0.19")])],"isStart":true})});
            fillet(context, id + "F15", {"entities" : qUnion([Q0, Q1, Q2, Q3, Q4, Q5, Q6, Q7, Q8, Q9, Q10, Q11, Q12, Q13, Q14, Q15, Q16, Q17, Q18, Q19, Q20, Q21, Q22, Q23, Q24, Q25, Q26, Q27, Q28, Q29, Q30, Q31, Q32, Q33, Q34, Q35, Q36, Q37, Q38]), "radius" : 1 * mm, "tangentPropagation" : true, "allowEdgeOverflow" : false});
        }
        {
            var Q0;
            Q0=makeQuery(id+"F5.boolean.opBoolean","COPY",EDGE,{"derivedFrom":makeQuery(id+"F5.opExtrude","SWEPT_EDGE",EDGE,{"disambiguationData":[OSD([sQuery(id+"F4.wireOp",EDGE,"E2.bottom"),sQuery(id+"F4.wireOp",EDGE,"E2.right")])]})});
            var Q1;
            Q1=makeQuery(id+"F5.boolean.opBoolean","COPY",EDGE,{"derivedFrom":makeQuery(id+"F5.opExtrude","SWEPT_EDGE",EDGE,{"disambiguationData":[OSD([sQuery(id+"F4.wireOp",EDGE,"E2.bottom"),sQuery(id+"F4.wireOp",EDGE,"E2.left")])]})});
            var Q2;
            Q2=makeQuery(id+"F5.boolean.opBoolean","COPY",EDGE,{"derivedFrom":makeQuery(id+"F5.opExtrude","CAP_EDGE",EDGE,{"disambiguationData":[OSD([sQuery(id+"F4.wireOp",EDGE,"E2.bottom")])],"isStart":false})});
            var Q3;
            Q3=makeQuery(id+"F5.boolean.opBoolean","COPY",EDGE,{"derivedFrom":makeQuery(id+"F5.opExtrude","CAP_EDGE",EDGE,{"disambiguationData":[OSD([sQuery(id+"F4.wireOp",EDGE,"E2.left")])],"isStart":false})});
            var Q4;
            Q4=makeQuery(id+"F5.boolean.opBoolean","COPY",EDGE,{"derivedFrom":makeQuery(id+"F5.opExtrude","CAP_EDGE",EDGE,{"disambiguationData":[OSD([sQuery(id+"F4.wireOp",EDGE,"E2.right")])],"isStart":false})});
            var Q5;
            Q5=makeQuery(id+"F5.boolean.opBoolean","COPY",EDGE,{"derivedFrom":makeQuery(id+"F5.opExtrude","CAP_EDGE",EDGE,{"disambiguationData":[OSD([sQuery(id+"F4.wireOp",EDGE,"E2.top")])],"isStart":false})});
            var Q6;
            Q6=makeQuery(id+"F5.boolean.opBoolean","COPY",EDGE,{"derivedFrom":makeQuery(id+"F5.opExtrude","SWEPT_EDGE",EDGE,{"disambiguationData":[OSD([sQuery(id+"F4.wireOp",EDGE,"E2.top"),sQuery(id+"F4.wireOp",EDGE,"E2.right")])]})});
            var Q7;
            Q7=makeQuery(id+"F5.boolean.opBoolean","COPY",EDGE,{"derivedFrom":makeQuery(id+"F5.opExtrude","SWEPT_EDGE",EDGE,{"disambiguationData":[OSD([sQuery(id+"F4.wireOp",EDGE,"E2.top"),sQuery(id+"F4.wireOp",EDGE,"E2.left")])]})});
            var Q8;
            Q8=makeQuery(id+"F2.opExtrude","CAP_EDGE",EDGE,{"disambiguationData":[OSD([sQuery(id+"F1.wireOp",EDGE,"E0.top")])],"isStart":true});
            var Q9;
            Q9=makeQuery(id+"F6.boolean.opBoolean","MERGE",EDGE,{"derivedFrom":[makeQuery(id+"F2.opExtrude","CAP_EDGE",EDGE,{"disambiguationData":[OSD([sQuery(id+"F1.wireOp",EDGE,"E0.right")])],"isStart":true}),makeQuery(id+"F6.opExtrude","SWEPT_EDGE",EDGE,{"disambiguationData":[OSD([sQuery(id+"F3.wireOp",EDGE,"E1.bottom"),sQuery(id+"F3.wireOp",EDGE,"E1.right")])]})]});
            var Q10;
            Q10=makeQuery(id+"F6.boolean.opBoolean","MERGE",EDGE,{"derivedFrom":[makeQuery(id+"F2.opExtrude","CAP_EDGE",EDGE,{"disambiguationData":[OSD([sQuery(id+"F1.wireOp",EDGE,"E0.left")])],"isStart":true}),makeQuery(id+"F6.opExtrude","SWEPT_EDGE",EDGE,{"disambiguationData":[OSD([sQuery(id+"F3.wireOp",EDGE,"E1.bottom"),sQuery(id+"F3.wireOp",EDGE,"E1.left")])]})]});
            var Q11;
            Q11=makeQuery(id+"F6.opExtrude","CAP_EDGE",EDGE,{"disambiguationData":[OSD([sQuery(id+"F3.wireOp",EDGE,"E1.bottom")])],"isStart":false});
            var Q12;
            Q12=makeQuery(id+"F6.opExtrude","CAP_EDGE",EDGE,{"disambiguationData":[OSD([sQuery(id+"F3.wireOp",EDGE,"E1.left")])],"isStart":false});
            var Q13;
            Q13=makeQuery(id+"F2.opExtrude","SWEPT_EDGE",EDGE,{"disambiguationData":[OSD([sQuery(id+"F1.wireOp",EDGE,"E0.top"),sQuery(id+"F1.wireOp",EDGE,"E0.left")])]});
            var Q14;
            Q14=makeQuery(id+"F2.opExtrude","SWEPT_EDGE",EDGE,{"disambiguationData":[OSD([sQuery(id+"F1.wireOp",EDGE,"E0.top"),sQuery(id+"F1.wireOp",EDGE,"E0.right")])]});
            var Q15;
            Q15=makeQuery(id+"F6.opExtrude","CAP_EDGE",EDGE,{"disambiguationData":[OSD([sQuery(id+"F3.wireOp",EDGE,"E1.right")])],"isStart":false});
            fillet(context, id + "F16", {"entities" : qUnion([Q0, Q1, Q2, Q3, Q4, Q5, Q6, Q7, Q8, Q9, Q10, Q11, Q12, Q13, Q14, Q15]), "radius" : 5 * mm, "tangentPropagation" : true, "allowEdgeOverflow" : false});
        }
        {
            var Q0;
            Q0=makeQuery(id+"F6.boolean.opBoolean","MERGE",FACE,{"derivedFrom":[makeQuery(id+"F2.opExtrude","CAP_FACE",FACE,{"disambiguationData":[OSD([sQuery(id+"F1.wireOp",EDGE,"E0.bottom"),sQuery(id+"F1.wireOp",EDGE,"E0.top"),sQuery(id+"F1.wireOp",EDGE,"E0.left"),sQuery(id+"F1.wireOp",EDGE,"E0.right")])],"isStart":true}),makeQuery(id+"F6.opExtrude","SWEPT_FACE",FACE,{"disambiguationData":[OSD([sQuery(id+"F3.wireOp",EDGE,"E1.bottom")])]})]});
            var sketch = newSketch(context, id + "F17", { "sketchPlane" : qUnion([Q0])});
            skCircle(sketch, "E51", {"center": v(0, 0) * mm, "radius": 5 * mm});
            skCircle(sketch, "E52", {"center": v(0, 11) * mm, "radius": 2 * mm});
            skCircle(sketch, "E53", {"center": v(0, 21) * mm, "radius": 3.5 * mm});
            skCircle(sketch, "E54.1.0", {"center": v(-11.35, 17.67) * mm, "radius": 3.5 * mm});
            skCircle(sketch, "E54.2.0", {"center": v(-19.1, 8.72) * mm, "radius": 3.5 * mm});
            skCircle(sketch, "E54.3.0", {"center": v(-20.79, -2.99) * mm, "radius": 3.5 * mm});
            skCircle(sketch, "E54.4.0", {"center": v(-15.87, -13.75) * mm, "radius": 3.5 * mm});
            skCircle(sketch, "E54.5.0", {"center": v(-5.92, -20.15) * mm, "radius": 3.5 * mm});
            skCircle(sketch, "E54.6.0", {"center": v(5.92, -20.15) * mm, "radius": 3.5 * mm});
            skCircle(sketch, "E55.1.0", {"center": v(-8.6, 6.86) * mm, "radius": 2 * mm});
            skCircle(sketch, "E55.2.0", {"center": v(-10.72, -2.45) * mm, "radius": 2 * mm});
            skCircle(sketch, "E55.3.0", {"center": v(-4.77, -9.91) * mm, "radius": 2 * mm});
            skCircle(sketch, "E55.4.0", {"center": v(4.77, -9.91) * mm, "radius": 2 * mm});
            skCircle(sketch, "E55.5.0", {"center": v(10.72, -2.45) * mm, "radius": 2 * mm});
            skCircle(sketch, "E55.6.0", {"center": v(8.6, 6.86) * mm, "radius": 2 * mm});
            skCircle(sketch, "E56.1.7.0", {"center": v(15.87, -13.75) * mm, "radius": 3.5 * mm});
            skCircle(sketch, "E56.1.8.0", {"center": v(20.79, -2.99) * mm, "radius": 3.5 * mm});
            skCircle(sketch, "E57.1.9.0", {"center": v(19.1, 8.72) * mm, "radius": 3.5 * mm});
            skCircle(sketch, "E57.1.10.0", {"center": v(11.35, 17.67) * mm, "radius": 3.5 * mm});
            skSolve(sketch);
        }
        {
            var Q0;
            Q0=qSketchRegion(id+"F17",true);
            extrude(context, id + "F18", {"entities" : qUnion([Q0]), "operationType" : NewBodyOperationType.REMOVE, "endBound" : BoundingType.UP_TO_NEXT, "oppositeDirection" : true, "depth" : 25 * mm, "offsetDistance" : 25 * mm, "hasDraft" : true, "draftAngle" : 3 * degree, "draftPullDirection" : true});
        }
        {
            var Q0;
            Q0=makeQuery(id+"F6.opExtrude","CAP_FACE",FACE,{"disambiguationData":[OSD([sQuery(id+"F3.wireOp",EDGE,"E1.bottom"),sQuery(id+"F3.wireOp",EDGE,"E1.top"),sQuery(id+"F3.wireOp",EDGE,"E1.left"),sQuery(id+"F3.wireOp",EDGE,"E1.right")])],"isStart":false});
            var sketch = newSketch(context, id + "F19", { "sketchPlane" : qUnion([Q0])});
            skLineSegment(sketch, "E58.bottom", {"start": v(-60, 120) * mm, "end": v(-17, 120) * mm});
            skLineSegment(sketch, "E58.top", {"start": v(-60, 241) * mm, "end": v(60, 241) * mm});
            skLineSegment(sketch, "E58.left", {"start": v(-60, 120) * mm, "end": v(-60, 241) * mm});
            skLineSegment(sketch, "E58.right", {"start": v(60, 120) * mm, "end": v(60, 241) * mm});
            skLineSegment(sketch, "E59", {"start": v(0, -10.58) * mm, "end": v(0, 289.25) * mm, "construction": true});
            skPoint(sketch, "E59.startSnap0", {"position": v(0, 129) * mm});
            skLineSegment(sketch, "E60.trimOffspring", {"start": v(-17, 120) * mm, "end": v(-60, 120) * mm});
            skLineSegment(sketch, "E61.MirrorCS", {"start": v(60, 120) * mm, "end": v(17, 120) * mm});
            skLineSegment(sketch, "E62", {"start": v(-17, 120) * mm, "end": v(-17, 70) * mm});
            skLineSegment(sketch, "E63", {"start": v(-17, 70) * mm, "end": v(17, 70) * mm});
            skLineSegment(sketch, "E64", {"start": v(17, 70) * mm, "end": v(17, 120) * mm});
            skLineSegment(sketch, "E65.bottom", {"start": v(-40, 70) * mm, "end": v(40, 70) * mm});
            skLineSegment(sketch, "E65.top", {"start": v(-40, 120) * mm, "end": v(40, 120) * mm});
            skLineSegment(sketch, "E65.left", {"start": v(-40, 70) * mm, "end": v(-40, 120) * mm});
            skLineSegment(sketch, "E65.right", {"start": v(40, 70) * mm, "end": v(40, 120) * mm});
            skSolve(sketch);
        }
        {
            var Q0;
            {var subQ0=sQuery(id+"F19.wireOp",EDGE,"E62");Q0=makeQuery(id+"F19.imprint","IMPRINT",FACE,{"disambiguationData":[TD([[makeQuery(id+"F19.imprint","IMPRINT",EDGE,{"derivedFrom":subQ0}),1.0]])]});}
            var Q1;
            {var subQ2=sQuery(id+"F3.wireOp",EDGE,"E1.top");var subQ16=makeQuery(id+"F10.boolean.opBoolean","MERGE",EDGE,{"derivedFrom":[makeQuery(id+"F6.opExtrude","CAP_EDGE",EDGE,{"disambiguationData":[OSD([subQ2])],"isStart":false}),makeQuery(id+"F10.opExtrude","CAP_EDGE",EDGE,{"disambiguationData":[OSD([sQuery(id+"F9.wireOp",EDGE,"E46.bottom")])],"isStart":true})]});Q1=makeQuery(id+"F19.imprint","IMPRINT",FACE,{"disambiguationData":[TD([[makeQuery(id+"F19.imprint","IMPRINT",EDGE,{"derivedFrom":subQ16}),-1.0]])]});}
            var Q2;
            Q2=makeQuery(id+"F19.imprint","IMPRINT",FACE,{"disambiguationData":[TD([[makeQuery(id+"F19.imprint","IMPRINT",EDGE,{"derivedFrom":sQuery(id+"F19.wireOp",EDGE,"E58.top")}),-1.0]])]});
            extrude(context, id + "F20", {"entities" : qUnion([Q0, Q1, Q2]), "operationType" : NewBodyOperationType.REMOVE, "oppositeDirection" : true, "depth" : 10 * mm, "offsetDistance" : 25 * mm});
        }
        {
            var Q0;
            {var subQ3=sQuery(id+"F19.wireOp",EDGE,"E65.left");Q0=makeQuery(id+"F19.imprint","IMPRINT",FACE,{"disambiguationData":[TD([[makeQuery(id+"F19.imprint","IMPRINT",EDGE,{"derivedFrom":subQ3}),1.0]])]});}
            var sketch = newSketch(context, id + "F21", { "sketchPlane" : qUnion([Q0])});
            skLineSegment(sketch, "E66.bottom", {"start": v(-40, 120) * mm, "end": v(40, 120) * mm});
            skLineSegment(sketch, "E66.top", {"start": v(-40, 65) * mm, "end": v(40, 65) * mm});
            skLineSegment(sketch, "E66.left", {"start": v(-40, 120) * mm, "end": v(-40, 65) * mm});
            skLineSegment(sketch, "E66.right", {"start": v(40, 120) * mm, "end": v(40, 65) * mm});
            skSolve(sketch);
        }
        {
            var Q0;
            Q0=qSketchRegion(id+"F21",true);
            extrude(context, id + "F22", {"entities" : qUnion([Q0]), "operationType" : NewBodyOperationType.ADD, "depth" : 10 * mm, "offsetDistance" : 25 * mm});
        }
        {
            var Q0;
            Q0=makeQuery(id+"F10.opExtrude","CAP_FACE",FACE,{"disambiguationData":[OSD([sQuery(id+"F9.wireOp",EDGE,"E46.bottom"),sQuery(id+"F9.wireOp",EDGE,"E46.top"),sQuery(id+"F9.wireOp",EDGE,"E46.left"),sQuery(id+"F9.wireOp",EDGE,"E46.right")])],"isStart":true});
            var sketch = newSketch(context, id + "F23", { "sketchPlane" : qUnion([Q0])});
            skLineSegment(sketch, "E67.bottom", {"start": v(81.46, 72.09) * mm, "end": v(-70.4, 72.09) * mm});
            skLineSegment(sketch, "E67.top", {"start": v(81.46, -110.53) * mm, "end": v(-70.4, -110.53) * mm});
            skLineSegment(sketch, "E67.left", {"start": v(81.46, 72.09) * mm, "end": v(81.46, -110.53) * mm});
            skLineSegment(sketch, "E67.right", {"start": v(-70.4, 72.09) * mm, "end": v(-70.4, -110.53) * mm});
            skSolve(sketch);
        }
        {
            var Q0;
            Q0 = qSketchRegion(id + "F23", true);
            extrude(context, id + "F24", {"entities" : qUnion([Q0]), "operationType" : NewBodyOperationType.REMOVE, "endBound" : BoundingType.UP_TO_NEXT, "oppositeDirection" : true, "depth" : 25 * mm, "offsetDistance" : 25 * mm});
        }
        {
            var Q0;
            Q0=makeQuery(id+"F20.boolean.opBoolean","COPY",EDGE,{"derivedFrom":makeQuery(id+"F20.opExtrude","CAP_EDGE",EDGE,{"disambiguationData":[OSD([sQuery(id+"F19.wireOp",EDGE,"E64")])],"isStart":false})});
            var Q1;
            Q1=makeQuery(id+"F20.boolean.opBoolean","COPY",EDGE,{"derivedFrom":makeQuery(id+"F20.opExtrude","CAP_EDGE",EDGE,{"disambiguationData":[OSD([sQuery(id+"F19.wireOp",EDGE,"E64")])],"isStart":true})});
            var Q2;
            Q2=makeQuery(id+"F20.boolean.opBoolean","COPY",FACE,{"derivedFrom":makeQuery(id+"F20.opExtrude","SWEPT_FACE",FACE,{"disambiguationData":[OSD([sQuery(id+"F19.wireOp",EDGE,"E65.bottom")])]})});
            var Q3;
            Q3=makeQuery(id+"F20.boolean.opBoolean","COPY",EDGE,{"derivedFrom":makeQuery(id+"F20.opExtrude","CAP_EDGE",EDGE,{"disambiguationData":[OSD([sQuery(id+"F19.wireOp",EDGE,"E62")])],"isStart":false})});
            var Q4;
            Q4=makeQuery(id+"F20.boolean.opBoolean","COPY",EDGE,{"derivedFrom":makeQuery(id+"F20.opExtrude","CAP_EDGE",EDGE,{"disambiguationData":[OSD([sQuery(id+"F19.wireOp",EDGE,"E62")])],"isStart":true})});
            fillet(context, id + "F25", {"entities" : qUnion([Q0, Q1, Q2, Q3, Q4]), "radius" : 3 * mm, "tangentPropagation" : true, "allowEdgeOverflow" : false});
        }
        {
            var Q0;
            Q0=makeQuery(id+"F2.opExtrude","SWEPT_FACE",FACE,{"disambiguationData":[OSD([sQuery(id+"F1.wireOp",EDGE,"E0.top")])]});
            var sketch = newSketch(context, id + "F26", { "sketchPlane" : qUnion([Q0])});
            skCircle(sketch, "E68", {"center": v(0, 70) * mm, "radius": 20 * mm});
            skSolve(sketch);
        }
        {
            var Q0;
            Q0=makeQuery(id+"F26.imprint","IMPRINT",FACE,{"disambiguationData":[TD([[makeQuery(id+"F26.imprint","IMPRINT",EDGE,{"derivedFrom":sQuery(id+"F26.wireOp",EDGE,"E68")}),1.0]])]});
            extrude(context, id + "F27", {"entities" : qUnion([Q0]), "operationType" : NewBodyOperationType.REMOVE, "oppositeDirection" : true, "depth" : 5 * mm, "offsetDistance" : 25 * mm});
        }
        {
            var Q0;
            Q0=makeQuery(id+"F26.imprint","IMPRINT",FACE,{"disambiguationData":[TD([[makeQuery(id+"F26.imprint","IMPRINT",EDGE,{"derivedFrom":sQuery(id+"F26.wireOp",EDGE,"E68")}),-1.0]])]});
            var sketch = newSketch(context, id + "F28", { "sketchPlane" : qUnion([Q0])});
            skCircle(sketch, "E69", {"center": v(120, 70) * mm, "radius": 20 * mm});
            skSolve(sketch);
        }
        {
            var Q0;
            Q0=makeQuery(id+"F28.imprint","IMPRINT",FACE,{"disambiguationData":[TD([[makeQuery(id+"F28.imprint","IMPRINT",EDGE,{"derivedFrom":sQuery(id+"F28.wireOp",EDGE,"E69")}),1.0]])]});
            extrude(context, id + "F29", {"entities" : qUnion([Q0]), "depth" : 5 * mm, "offsetDistance" : 25 * mm});
        }
        {
            var Q0;
            Q0=makeQuery(id+"F29.opExtrude","CAP_FACE",FACE,{"disambiguationData":[OSD([sQuery(id+"F28.wireOp",EDGE,"E69")])],"isStart":false});
            var sketch = newSketch(context, id + "F30", { "sketchPlane" : qUnion([Q0])});
            skArc(sketch, "E70.0", {"start": v(114, 50.92) * mm, "mid": v(120, 50) * mm, "end": v(126, 50.92) * mm});
            skLineSegment(sketch, "E71.left", {"start": v(114, 89.08) * mm, "end": v(114, 50.92) * mm});
            skLineSegment(sketch, "E71.right", {"start": v(126, 89.08) * mm, "end": v(126, 50.92) * mm});
            skArc(sketch, "E72.trimOffspring", {"start": v(126, 89.08) * mm, "mid": v(120, 90) * mm, "end": v(114, 89.08) * mm});
            skSolve(sketch);
        }
        {
            var Q0;
            Q0 = qSketchRegion(id + "F30", true);
            extrude(context, id + "F31", {"entities" : qUnion([Q0]), "operationType" : NewBodyOperationType.ADD, "depth" : 15 * mm, "offsetDistance" : 25 * mm});
        }
        {
            var Q0;
            Q0=makeQuery(id+"F31.opExtrude","CAP_EDGE",EDGE,{"disambiguationData":[OSD([sQuery(id+"F30.wireOp",EDGE,"E71.right")])],"isStart":false});
            var Q1;
            Q1=makeQuery(id+"F31.opExtrude","CAP_EDGE",EDGE,{"disambiguationData":[OSD([sQuery(id+"F30.wireOp",EDGE,"E72.trimOffspring")])],"isStart":false});
            var Q2;
            Q2=makeQuery(id+"F31.opExtrude","CAP_EDGE",EDGE,{"disambiguationData":[OSD([sQuery(id+"F30.wireOp",EDGE,"E71.left")])],"isStart":false});
            var Q3;
            Q3=makeQuery(id+"F31.opExtrude","CAP_EDGE",EDGE,{"disambiguationData":[OSD([sQuery(id+"F30.wireOp",EDGE,"E70.0")])],"isStart":false});
            var Q4;
            Q4=makeQuery(id+"F31.opExtrude","SWEPT_EDGE",EDGE,{"disambiguationData":[OSD([sQuery(id+"F28.wireOp",EDGE,"E69"),sQuery(id+"F30.wireOp",EDGE,"E70.0"),sQuery(id+"F30.wireOp",EDGE,"E71.left")])]});
            var Q5;
            Q5=makeQuery(id+"F31.opExtrude","SWEPT_EDGE",EDGE,{"disambiguationData":[OSD([sQuery(id+"F28.wireOp",EDGE,"E69"),sQuery(id+"F30.wireOp",EDGE,"E70.0"),sQuery(id+"F30.wireOp",EDGE,"E71.right")])]});
            var Q6;
            Q6=makeQuery(id+"F31.opExtrude","SWEPT_EDGE",EDGE,{"disambiguationData":[OSD([sQuery(id+"F28.wireOp",EDGE,"E69"),sQuery(id+"F30.wireOp",EDGE,"E71.right"),sQuery(id+"F30.wireOp",EDGE,"E72.trimOffspring")])]});
            var Q7;
            Q7=makeQuery(id+"F31.opExtrude","SWEPT_EDGE",EDGE,{"disambiguationData":[OSD([sQuery(id+"F28.wireOp",EDGE,"E69"),sQuery(id+"F30.wireOp",EDGE,"E71.left"),sQuery(id+"F30.wireOp",EDGE,"E72.trimOffspring")])]});
            fillet(context, id + "F32", {"entities" : qUnion([Q0, Q1, Q2, Q3, Q4, Q5, Q6, Q7]), "radius" : 5 * mm, "tangentPropagation" : true, "allowEdgeOverflow" : false});
        }
    });
